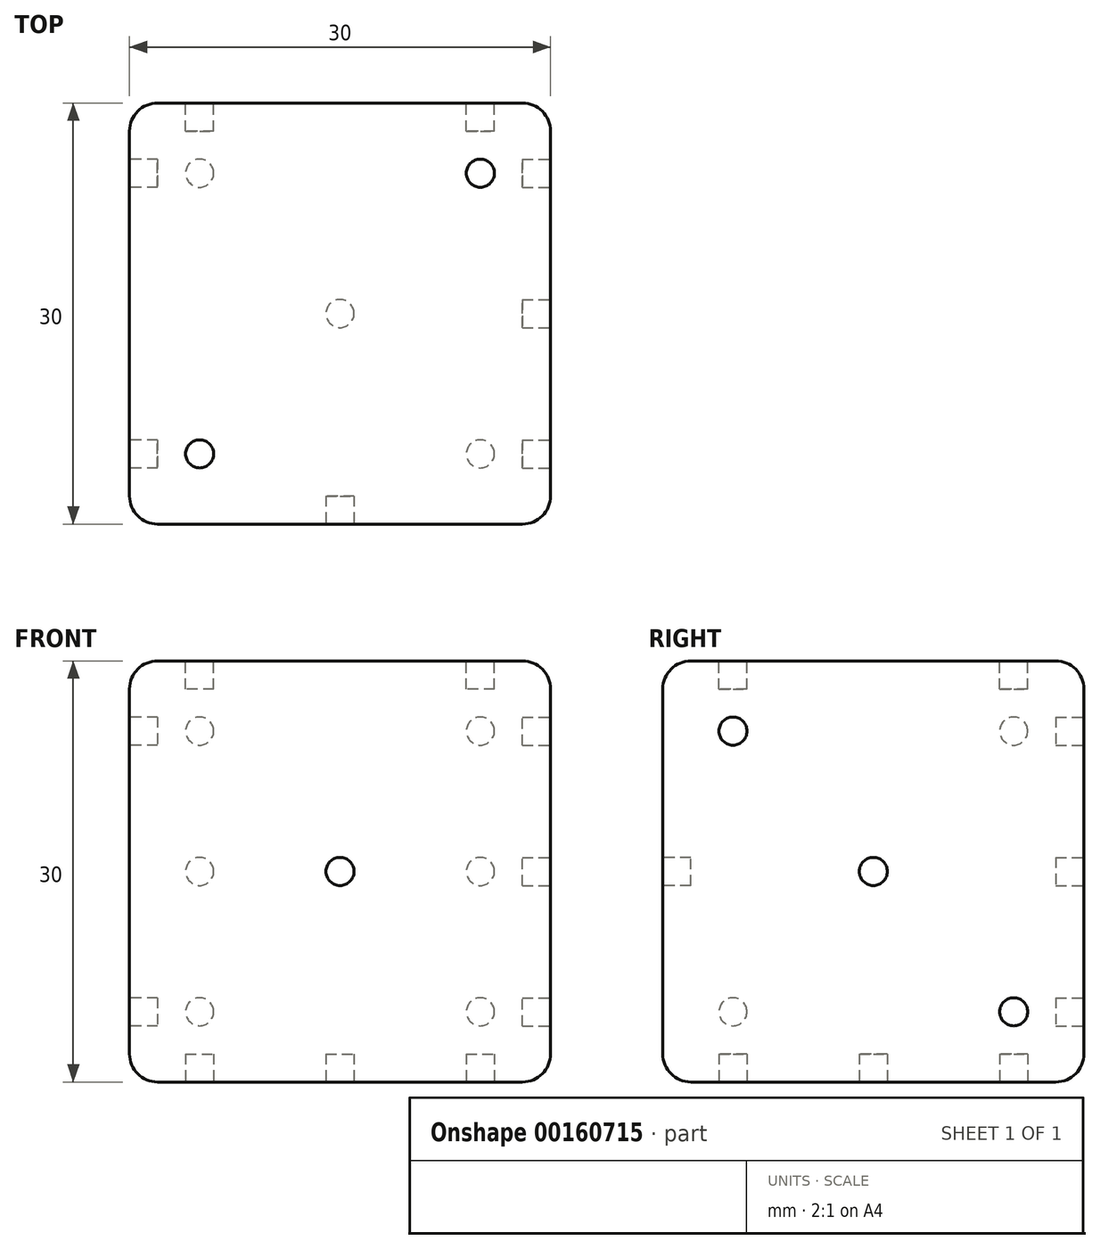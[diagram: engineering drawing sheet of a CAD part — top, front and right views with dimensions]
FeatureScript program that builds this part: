
annotation { "Feature Type Name" : "Feature", "Feature Type Description" : "" }
export const myFeature = defineFeature(function(context is Context, id is Id, definition is map)
    precondition{}
    {
        {
            var Q0;
            Q0=qCreatedBy(makeId("Front.planeOp"),FACE);
            var sketch = newSketch(context, id + "F0", { "sketchPlane" : qUnion([Q0])});
            skLineSegment(sketch, "E0.bottom", {"start": v(15, -15) * mm, "end": v(-15, -15) * mm});
            skLineSegment(sketch, "E0.top", {"start": v(15, 15) * mm, "end": v(-15, 15) * mm});
            skLineSegment(sketch, "E0.left", {"start": v(15, -15) * mm, "end": v(15, 15) * mm});
            skLineSegment(sketch, "E0.right", {"start": v(-15, -15) * mm, "end": v(-15, 15) * mm});
            skPoint(sketch, "E0.middle", {"position": v(0, 0) * mm});
            skSolve(sketch);
        }
        {
            var Q0;
            Q0=makeQuery(id+"F0.imprint","IMPRINT",FACE,{"disambiguationData":[TD([[makeQuery(id+"F0.imprint","IMPRINT",EDGE,{"derivedFrom":sQuery(id+"F0.wireOp",EDGE,"E0.bottom")}),-1.0]])]});
            extrude(context, id + "F1", {"entities" : qUnion([Q0]), "endBound" : BoundingType.SYMMETRIC, "depth" : 30 * mm});
        }
        {
            var Q0;
            Q0=qCreatedBy(makeId("Right.planeOp"),FACE);
            var sketch = newSketch(context, id + "F2", { "sketchPlane" : qUnion([Q0])});
            skLineSegment(sketch, "E1", {"start": v(-17.73, 0) * mm, "end": v(18.5, 0) * mm});
            skSolve(sketch);
        }
        {
            var Q0;
            Q0=makeQuery(id+"F1.opExtrude","SWEPT_BODY",BODY,{"disambiguationData":[OSD([sQuery(id+"F0.wireOp",EDGE,"E0.bottom"),sQuery(id+"F0.wireOp",EDGE,"E0.top"),sQuery(id+"F0.wireOp",EDGE,"E0.left"),sQuery(id+"F0.wireOp",EDGE,"E0.right")])]});
            var Q1;
            Q1=sQuery(id+"F2.wireOp",EDGE,"E1");
            transform(context, id + "F3", {"entities" : qUnion([Q0]), "transformType" : TransformType.ROTATION, "transformAxis" : qUnion([Q1]), "angle" : 270 * degree, "makeCopy" : false});
        }
        {
            var Q0;
            Q0=makeQuery(id+"F1.opExtrude","SWEPT_EDGE",EDGE,{"disambiguationData":[OSD([sQuery(id+"F0.wireOp",EDGE,"E0.top"),sQuery(id+"F0.wireOp",EDGE,"E0.right")])]});
            var Q1;
            Q1=makeQuery(id+"F1.opExtrude","CAP_EDGE",EDGE,{"disambiguationData":[OSD([sQuery(id+"F0.wireOp",EDGE,"E0.right")])],"isStart":false});
            var Q2;
            Q2=makeQuery(id+"F1.opExtrude","CAP_EDGE",EDGE,{"disambiguationData":[OSD([sQuery(id+"F0.wireOp",EDGE,"E0.top")])],"isStart":false});
            var Q3;
            Q3=makeQuery(id+"F1.opExtrude","CAP_EDGE",EDGE,{"disambiguationData":[OSD([sQuery(id+"F0.wireOp",EDGE,"E0.left")])],"isStart":false});
            var Q4;
            Q4=makeQuery(id+"F1.opExtrude","SWEPT_EDGE",EDGE,{"disambiguationData":[OSD([sQuery(id+"F0.wireOp",EDGE,"E0.top"),sQuery(id+"F0.wireOp",EDGE,"E0.left")])]});
            var Q5;
            Q5=makeQuery(id+"F1.opExtrude","CAP_EDGE",EDGE,{"disambiguationData":[OSD([sQuery(id+"F0.wireOp",EDGE,"E0.top")])],"isStart":true});
            var Q6;
            Q6=makeQuery(id+"F1.opExtrude","SWEPT_EDGE",EDGE,{"disambiguationData":[OSD([sQuery(id+"F0.wireOp",EDGE,"E0.bottom"),sQuery(id+"F0.wireOp",EDGE,"E0.left")])]});
            var Q7;
            Q7=makeQuery(id+"F1.opExtrude","CAP_EDGE",EDGE,{"disambiguationData":[OSD([sQuery(id+"F0.wireOp",EDGE,"E0.bottom")])],"isStart":false});
            var Q8;
            Q8=makeQuery(id+"F1.opExtrude","SWEPT_EDGE",EDGE,{"disambiguationData":[OSD([sQuery(id+"F0.wireOp",EDGE,"E0.bottom"),sQuery(id+"F0.wireOp",EDGE,"E0.right")])]});
            var Q9;
            Q9=makeQuery(id+"F1.opExtrude","CAP_EDGE",EDGE,{"disambiguationData":[OSD([sQuery(id+"F0.wireOp",EDGE,"E0.right")])],"isStart":true});
            var Q10;
            Q10=makeQuery(id+"F1.opExtrude","CAP_EDGE",EDGE,{"disambiguationData":[OSD([sQuery(id+"F0.wireOp",EDGE,"E0.bottom")])],"isStart":true});
            var Q11;
            Q11=makeQuery(id+"F1.opExtrude","CAP_EDGE",EDGE,{"disambiguationData":[OSD([sQuery(id+"F0.wireOp",EDGE,"E0.left")])],"isStart":true});
            fillet(context, id + "F4", {"entities" : qUnion([Q0, Q1, Q2, Q3, Q4, Q5, Q6, Q7, Q8, Q9, Q10, Q11]), "radius" : 2 * mm, "tangentPropagation" : true, "allowEdgeOverflow" : false});
        }
        {
            var Q0;
            Q0=makeQuery(id+"F1.opExtrude","CAP_FACE",FACE,{"disambiguationData":[OSD([sQuery(id+"F0.wireOp",EDGE,"E0.bottom"),sQuery(id+"F0.wireOp",EDGE,"E0.top"),sQuery(id+"F0.wireOp",EDGE,"E0.left"),sQuery(id+"F0.wireOp",EDGE,"E0.right")])],"isStart":false});
            var sketch = newSketch(context, id + "F5", { "sketchPlane" : qUnion([Q0])});
            skCircle(sketch, "E2", {"center": v(0, 0) * mm, "radius": 1 * mm});
            skSolve(sketch);
        }
        {
            var Q0;
            Q0 = qSketchRegion(id + "F5", true);
            extrude(context, id + "F6", {"entities" : qUnion([Q0]), "operationType" : NewBodyOperationType.REMOVE, "oppositeDirection" : true, "depth" : 2 * mm});
        }
        {
            var Q0;
            Q0=makeQuery(id+"F1.opExtrude","SWEPT_FACE",FACE,{"disambiguationData":[OSD([sQuery(id+"F0.wireOp",EDGE,"E0.top")])]});
            var sketch = newSketch(context, id + "F7", { "sketchPlane" : qUnion([Q0])});
            skCircle(sketch, "E3", {"center": v(-10, -10) * mm, "radius": 1 * mm});
            skCircle(sketch, "E4.MirrorC", {"center": v(10, -10) * mm, "radius": 1 * mm});
            skCircle(sketch, "E5.MirrorC", {"center": v(10, 10) * mm, "radius": 1 * mm});
            skCircle(sketch, "E6.MirrorC", {"center": v(-10, 10) * mm, "radius": 1 * mm});
            skSolve(sketch);
        }
        {
            var Q0;
            Q0 = qSketchRegion(id + "F7", true);
            extrude(context, id + "F8", {"entities" : qUnion([Q0]), "operationType" : NewBodyOperationType.REMOVE, "oppositeDirection" : true, "depth" : 2 * mm});
        }
        {
            var Q0;
            Q0=makeQuery(id+"F1.opExtrude","CAP_FACE",FACE,{"disambiguationData":[OSD([sQuery(id+"F0.wireOp",EDGE,"E0.bottom"),sQuery(id+"F0.wireOp",EDGE,"E0.top"),sQuery(id+"F0.wireOp",EDGE,"E0.left"),sQuery(id+"F0.wireOp",EDGE,"E0.right")])],"isStart":true});
            var sketch = newSketch(context, id + "F9", { "sketchPlane" : qUnion([Q0])});
            skCircle(sketch, "E7", {"center": v(-10, 10) * mm, "radius": 1 * mm});
            skCircle(sketch, "E8.MirrorC", {"center": v(-10, -10) * mm, "radius": 1 * mm});
            skLineSegment(sketch, "E9", {"start": v(-10, 10) * mm, "end": v(-10, -10) * mm});
            skCircle(sketch, "E10", {"center": v(-10, 0) * mm, "radius": 1 * mm});
            skCircle(sketch, "E11.MirrorC", {"center": v(10, 0) * mm, "radius": 1 * mm});
            skCircle(sketch, "E12.MirrorC", {"center": v(10, -10) * mm, "radius": 1 * mm});
            skCircle(sketch, "E13.MirrorC", {"center": v(10, 10) * mm, "radius": 1 * mm});
            skLineSegment(sketch, "E14.MirrorCS", {"start": v(10, 10) * mm, "end": v(10, -10) * mm});
            skSolve(sketch);
        }
        {
            var Q0;
            Q0 = qSketchRegion(id + "F9", true);
            extrude(context, id + "F10", {"entities" : qUnion([Q0]), "operationType" : NewBodyOperationType.REMOVE, "oppositeDirection" : true, "depth" : 2 * mm});
        }
        {
            var Q0;
            Q0=makeQuery(id+"F1.opExtrude","SWEPT_FACE",FACE,{"disambiguationData":[OSD([sQuery(id+"F0.wireOp",EDGE,"E0.bottom")])]});
            var sketch = newSketch(context, id + "F11", { "sketchPlane" : qUnion([Q0])});
            skCircle(sketch, "E15", {"center": v(-10, 10) * mm, "radius": 1 * mm});
            skCircle(sketch, "E16", {"center": v(10, -10) * mm, "radius": 1 * mm});
            skCircle(sketch, "E17", {"center": v(0, 0) * mm, "radius": 1 * mm});
            skSolve(sketch);
        }
        {
            var Q0;
            Q0 = qSketchRegion(id + "F11", true);
            extrude(context, id + "F12", {"entities" : qUnion([Q0]), "operationType" : NewBodyOperationType.REMOVE, "oppositeDirection" : true, "depth" : 2 * mm});
        }
        {
            var Q0;
            Q0=makeQuery(id+"F1.opExtrude","SWEPT_FACE",FACE,{"disambiguationData":[OSD([sQuery(id+"F0.wireOp",EDGE,"E0.left")])]});
            var sketch = newSketch(context, id + "F13", { "sketchPlane" : qUnion([Q0])});
            skCircle(sketch, "E18", {"center": v(-10, -10) * mm, "radius": 1 * mm});
            skCircle(sketch, "E19", {"center": v(10, 10) * mm, "radius": 1 * mm});
            skSolve(sketch);
        }
        {
            var Q0;
            Q0 = qSketchRegion(id + "F13", true);
            extrude(context, id + "F14", {"entities" : qUnion([Q0]), "operationType" : NewBodyOperationType.REMOVE, "oppositeDirection" : true, "depth" : 2 * mm});
        }
        {
            var Q0;
            Q0=makeQuery(id+"F1.opExtrude","SWEPT_FACE",FACE,{"disambiguationData":[OSD([sQuery(id+"F0.wireOp",EDGE,"E0.right")])]});
            var sketch = newSketch(context, id + "F15", { "sketchPlane" : qUnion([Q0])});
            skCircle(sketch, "E20", {"center": v(-10, 10) * mm, "radius": 1 * mm});
            skCircle(sketch, "E21.MirrorC", {"center": v(10, 10) * mm, "radius": 1 * mm});
            skCircle(sketch, "E22.MirrorC", {"center": v(10, -10) * mm, "radius": 1 * mm});
            skCircle(sketch, "E23.MirrorC", {"center": v(-10, -10) * mm, "radius": 1 * mm});
            skCircle(sketch, "E24", {"center": v(0, 0) * mm, "radius": 1 * mm});
            skSolve(sketch);
        }
        {
            var Q0;
            Q0 = qSketchRegion(id + "F15", true);
            extrude(context, id + "F16", {"entities" : qUnion([Q0]), "operationType" : NewBodyOperationType.REMOVE, "oppositeDirection" : true, "depth" : 2 * mm});
        }
    });
